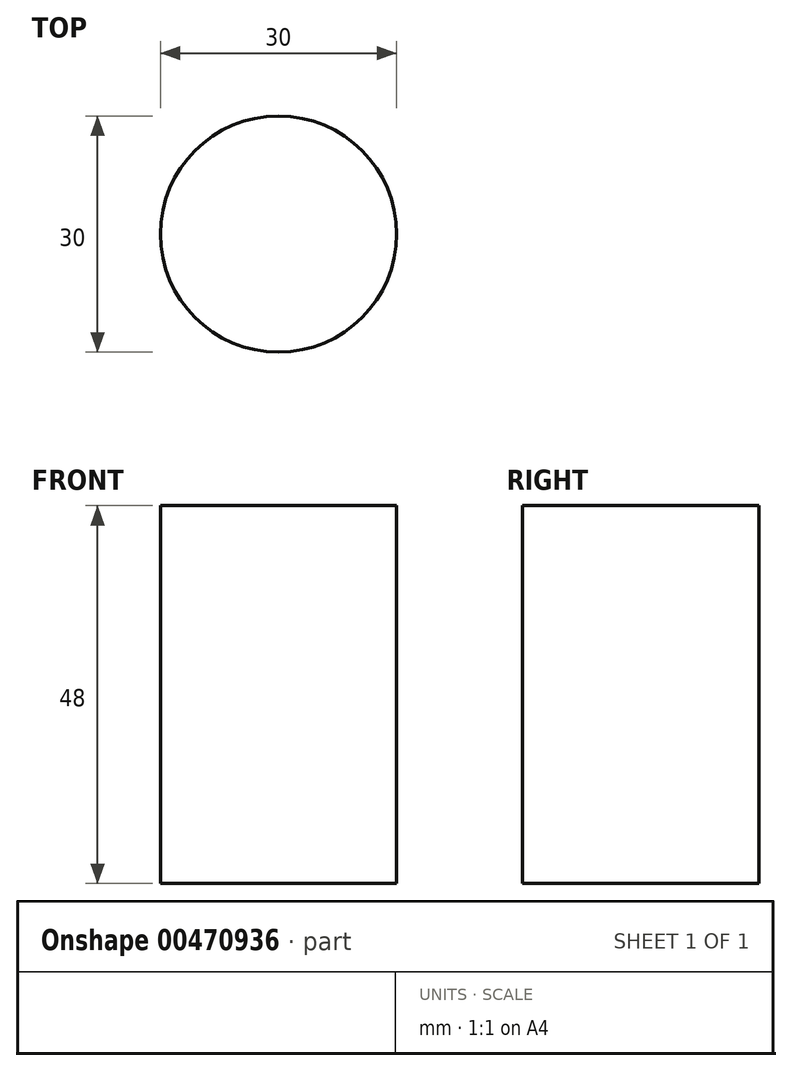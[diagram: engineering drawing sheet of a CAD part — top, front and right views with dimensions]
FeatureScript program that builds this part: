
annotation { "Feature Type Name" : "Feature", "Feature Type Description" : "" }
export const myFeature = defineFeature(function(context is Context, id is Id, definition is map)
    precondition{}
    {
        {
            var Q0;
            Q0=qCreatedBy(makeId("Top.planeOp"),FACE);
            var sketch = newSketch(context, id + "F0", { "sketchPlane" : qUnion([Q0])});
            skCircle(sketch, "E0", {"center": v(0, 0) * mm, "radius": 15 * mm});
            skSolve(sketch);
        }
        {
            var Q0;
            Q0 = qSketchRegion(id + "F0", true);
            extrude(context, id + "F1", {"entities" : qUnion([Q0]), "depth" : 48 * mm});
        }
    });
